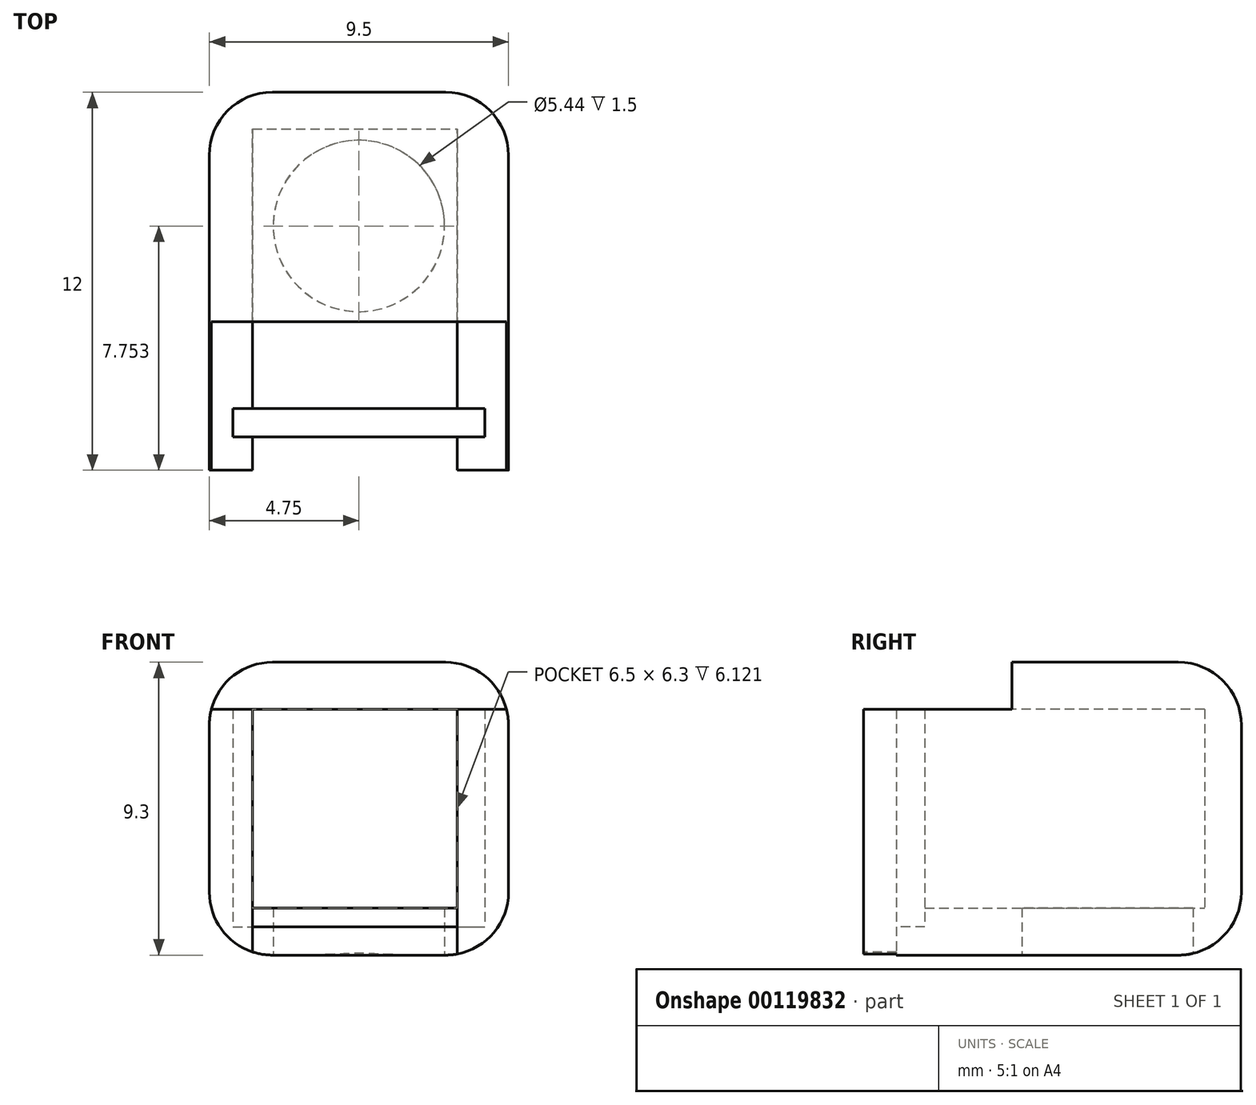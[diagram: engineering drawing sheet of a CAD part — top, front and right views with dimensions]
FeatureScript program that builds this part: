
annotation { "Feature Type Name" : "Feature", "Feature Type Description" : "" }
export const myFeature = defineFeature(function(context is Context, id is Id, definition is map)
    precondition{}
    {
        {
            var Q0;
            Q0=qCreatedBy(makeId("Top.planeOp"),FACE);
            var sketch = newSketch(context, id + "F0", { "sketchPlane" : qUnion([Q0])});
            skPoint(sketch, "E0.rect.middle", {"position": v(0, 0) * mm});
            skLineSegment(sketch, "E1.rect.bottom", {"start": v(-4.75, -1.5) * mm, "end": v(4.75, -1.5) * mm});
            skLineSegment(sketch, "E1.rect.top", {"start": v(-4.75, 1.5) * mm, "end": v(-3.38, 1.5) * mm});
            skLineSegment(sketch, "E1.rect.left", {"start": v(-4.75, -1.5) * mm, "end": v(-4.75, 1.5) * mm});
            skLineSegment(sketch, "E1.rect.right", {"start": v(4.75, -1.5) * mm, "end": v(4.75, 1.5) * mm});
            skLineSegment(sketch, "E2.rect.bottom", {"start": v(4, -0.45) * mm, "end": v(-4, -0.45) * mm});
            skLineSegment(sketch, "E2.rect.top", {"start": v(4, 0.45) * mm, "end": v(-4, 0.45) * mm});
            skLineSegment(sketch, "E2.rect.left", {"start": v(4, -0.45) * mm, "end": v(4, 0.45) * mm});
            skLineSegment(sketch, "E2.rect.right", {"start": v(-4, -0.45) * mm, "end": v(-4, 0.45) * mm});
            skLineSegment(sketch, "E3.rect.bottom", {"start": v(-3.12, -1.5) * mm, "end": v(3.38, -1.5) * mm});
            skLineSegment(sketch, "E4.trimOffspring", {"start": v(3.12, 1.5) * mm, "end": v(4.75, 1.5) * mm});
            skLineSegment(sketch, "E5", {"start": v(-3.38, 1.5) * mm, "end": v(3.12, 1.5) * mm, "construction": true});
            skLineSegment(sketch, "E6.bottom", {"start": v(4.75, 1.5) * mm, "end": v(-4.75, 1.5) * mm});
            skLineSegment(sketch, "E7.bottom", {"start": v(3.12, 1.5) * mm, "end": v(-4.75, 1.5) * mm});
            skLineSegment(sketch, "E8.bottom", {"start": v(-4.75, 1.5) * mm, "end": v(4.75, 1.5) * mm});
            skLineSegment(sketch, "E8.top", {"start": v(-4.75, 10.5) * mm, "end": v(4.75, 10.5) * mm});
            skLineSegment(sketch, "E8.left", {"start": v(-4.75, 1.5) * mm, "end": v(-4.75, 10.5) * mm});
            skLineSegment(sketch, "E8.right", {"start": v(4.75, 1.5) * mm, "end": v(4.75, 10.5) * mm});
            skLineSegment(sketch, "E9", {"start": v(-3.38, 1.5) * mm, "end": v(-3.38, 10.5) * mm});
            skLineSegment(sketch, "E10", {"start": v(3.12, 1.5) * mm, "end": v(3.12, 10.5) * mm});
            skLineSegment(sketch, "E11", {"start": v(4.75, 9.33) * mm, "end": v(-4.75, 9.33) * mm});
            skLineSegment(sketch, "E12", {"start": v(-3.38, 1.5) * mm, "end": v(-3.38, -1.5) * mm});
            skLineSegment(sketch, "E13", {"start": v(3.12, 1.5) * mm, "end": v(3.12, -1.5) * mm});
            skSolve(sketch);
        }
        {
            var Q0;
            {var subQ0=sQuery(id+"F0.wireOp",EDGE,"E6.right");Q0=makeQuery(id+"F0.imprint","IMPRINT",FACE,{"disambiguationData":[TD([[makeQuery(id+"F0.imprint","IMPRINT",EDGE,{"derivedFrom":subQ0}),-1.0]])]});}
            var Q1;
            Q1=makeQuery(id+"F0.imprint","IMPRINT",FACE,{"disambiguationData":[TD([[makeQuery(id+"F0.imprint","IMPRINT",EDGE,{"derivedFrom":sQuery(id+"F0.wireOp",EDGE,"E7.bottom")}),-1.0]])]});
            var Q2;
            {var subQ5=sQuery(id+"F0.wireOp",EDGE,"E7.bottom");Q2=makeQuery(id+"F0.imprint","IMPRINT",FACE,{"disambiguationData":[TD([[makeQuery(id+"F0.imprint","IMPRINT",EDGE,{"derivedFrom":subQ5}),1.0]])]});}
            var Q3;
            {var subQ8=sQuery(id+"F0.wireOp",EDGE,"E1.rect.right");Q3=makeQuery(id+"F0.imprint","IMPRINT",FACE,{"disambiguationData":[TD([[makeQuery(id+"F0.imprint","IMPRINT",EDGE,{"derivedFrom":subQ8}),1.0]])]});}
            var Q4;
            {var subQ5=sQuery(id+"F0.wireOp",EDGE,"E3.rect.bottom");Q4=makeQuery(id+"F0.imprint","IMPRINT",FACE,{"disambiguationData":[TD([[makeQuery(id+"F0.imprint","IMPRINT",EDGE,{"derivedFrom":subQ5}),1.0]])]});}
            var Q5;
            {var subQ4=sQuery(id+"F0.wireOp",EDGE,"E1.rect.left");Q5=makeQuery(id+"F0.imprint","IMPRINT",FACE,{"disambiguationData":[TD([[makeQuery(id+"F0.imprint","IMPRINT",EDGE,{"derivedFrom":subQ4}),-1.0]])]});}
            var Q6;
            {var subQ0=sQuery(id+"F0.wireOp",EDGE,"E6.left");Q6=makeQuery(id+"F0.imprint","IMPRINT",FACE,{"disambiguationData":[TD([[makeQuery(id+"F0.imprint","IMPRINT",EDGE,{"derivedFrom":subQ0}),1.0]])]});}
            var Q7;
            {var subQ0=sQuery(id+"F0.wireOp",EDGE,"E3.rect.right");var subQ1=sQuery(id+"F0.wireOp",EDGE,"E2.rect.bottom");var subQ2=makeQuery(id+"F0.imprint","INTERSECT",VERTEX,{"derivedFrom":[subQ1,subQ0]});Q7=makeQuery(id+"F0.imprint","IMPRINT",FACE,{"disambiguationData":[TD([[makeQuery(id+"F0.imprint","IMPRINT",EDGE,{"disambiguationData":[TD([[subQ2,-1.0]])],"derivedFrom":subQ1}),-1.0]])]});}
            var Q8;
            {var subQ0=sQuery(id+"F0.wireOp",EDGE,"E2.rect.right");Q8=makeQuery(id+"F0.imprint","IMPRINT",FACE,{"disambiguationData":[TD([[makeQuery(id+"F0.imprint","IMPRINT",EDGE,{"derivedFrom":subQ0}),-1.0]])]});}
            var Q9;
            {var subQ0=sQuery(id+"F0.wireOp",EDGE,"E2.rect.left");Q9=makeQuery(id+"F0.imprint","IMPRINT",FACE,{"disambiguationData":[TD([[makeQuery(id+"F0.imprint","IMPRINT",EDGE,{"derivedFrom":subQ0}),1.0]])]});}
            var Q10;
            {var subQ0=sQuery(id+"F0.wireOp",EDGE,"E8.left");var subQ5=sQuery(id+"F0.wireOp",EDGE,"E11");var subQ6=makeQuery(id+"F0.imprint","INTERSECT",VERTEX,{"derivedFrom":[subQ0,subQ5]});Q10=makeQuery(id+"F0.imprint","IMPRINT",FACE,{"disambiguationData":[TD([[makeQuery(id+"F0.imprint","IMPRINT",EDGE,{"disambiguationData":[TD([[subQ6,1.0]])],"derivedFrom":subQ5}),1.0]])]});}
            var Q11;
            {var subQ0=sQuery(id+"F0.wireOp",EDGE,"E8.left");var subQ1=sQuery(id+"F0.wireOp",EDGE,"E8.top");var subQ2=makeQuery(id+"F0.imprint","INTERSECT",VERTEX,{"derivedFrom":[subQ1,subQ0]});Q11=makeQuery(id+"F0.imprint","IMPRINT",FACE,{"disambiguationData":[TD([[makeQuery(id+"F0.imprint","IMPRINT",EDGE,{"disambiguationData":[TD([[subQ2,-1.0]])],"derivedFrom":subQ1}),-1.0]])]});}
            var Q12;
            {var subQ0=sQuery(id+"F0.wireOp",EDGE,"E9");var subQ1=sQuery(id+"F0.wireOp",EDGE,"E8.top");var subQ2=makeQuery(id+"F0.imprint","INTERSECT",VERTEX,{"derivedFrom":[subQ1,subQ0]});Q12=makeQuery(id+"F0.imprint","IMPRINT",FACE,{"disambiguationData":[TD([[makeQuery(id+"F0.imprint","IMPRINT",EDGE,{"disambiguationData":[TD([[subQ2,-1.0]])],"derivedFrom":subQ1}),-1.0]])]});}
            var Q13;
            {var subQ0=sQuery(id+"F0.wireOp",EDGE,"E8.right");var subQ1=sQuery(id+"F0.wireOp",EDGE,"E8.top");var subQ2=makeQuery(id+"F0.imprint","INTERSECT",VERTEX,{"derivedFrom":[subQ1,subQ0]});Q13=makeQuery(id+"F0.imprint","IMPRINT",FACE,{"disambiguationData":[TD([[makeQuery(id+"F0.imprint","IMPRINT",EDGE,{"disambiguationData":[TD([[subQ2,1.0]])],"derivedFrom":subQ1}),-1.0]])]});}
            var Q14;
            {var subQ0=sQuery(id+"F0.wireOp",EDGE,"E8.right");var subQ5=sQuery(id+"F0.wireOp",EDGE,"E11");var subQ6=makeQuery(id+"F0.imprint","INTERSECT",VERTEX,{"derivedFrom":[subQ0,subQ5]});Q14=makeQuery(id+"F0.imprint","IMPRINT",FACE,{"disambiguationData":[TD([[makeQuery(id+"F0.imprint","IMPRINT",EDGE,{"disambiguationData":[TD([[subQ6,-1.0]])],"derivedFrom":subQ5}),1.0]])]});}
            var Q15;
            {var subQ0=sQuery(id+"F0.wireOp",EDGE,"E3.rect.right");var subQ1=sQuery(id+"F0.wireOp",EDGE,"E2.rect.top");var subQ2=makeQuery(id+"F0.imprint","INTERSECT",VERTEX,{"derivedFrom":[subQ1,subQ0]});Q15=makeQuery(id+"F0.imprint","IMPRINT",FACE,{"disambiguationData":[TD([[makeQuery(id+"F0.imprint","IMPRINT",EDGE,{"disambiguationData":[TD([[subQ2,-1.0]])],"derivedFrom":subQ1}),-1.0]])]});}
            var Q16;
            {var subQ0=sQuery(id+"F0.wireOp",EDGE,"E9");var subQ5=sQuery(id+"F0.wireOp",EDGE,"E11");var subQ6=makeQuery(id+"F0.imprint","INTERSECT",VERTEX,{"derivedFrom":[subQ0,subQ5]});Q16=makeQuery(id+"F0.imprint","IMPRINT",FACE,{"disambiguationData":[TD([[makeQuery(id+"F0.imprint","IMPRINT",EDGE,{"disambiguationData":[TD([[subQ6,1.0]])],"derivedFrom":subQ5}),1.0]])]});}
            extrude(context, id + "F1", {"entities" : qUnion([Q0, Q1, Q2, Q3, Q4, Q5, Q6, Q7, Q8, Q9, Q10, Q11, Q12, Q13, Q14, Q15, Q16]), "depth" : 0.9 * mm});
        }
        {
            var Q0;
            {var subQ0=sQuery(id+"F0.wireOp",EDGE,"E6.left");Q0=makeQuery(id+"F0.imprint","IMPRINT",FACE,{"disambiguationData":[TD([[makeQuery(id+"F0.imprint","IMPRINT",EDGE,{"derivedFrom":subQ0}),1.0]])]});}
            var Q1;
            {var subQ0=sQuery(id+"F0.wireOp",EDGE,"E6.right");Q1=makeQuery(id+"F0.imprint","IMPRINT",FACE,{"disambiguationData":[TD([[makeQuery(id+"F0.imprint","IMPRINT",EDGE,{"derivedFrom":subQ0}),-1.0]])]});}
            var Q2;
            {var subQ5=sQuery(id+"F0.wireOp",EDGE,"E3.rect.bottom");Q2=makeQuery(id+"F0.imprint","IMPRINT",FACE,{"disambiguationData":[TD([[makeQuery(id+"F0.imprint","IMPRINT",EDGE,{"derivedFrom":subQ5}),1.0]])]});}
            var Q3;
            {var subQ4=sQuery(id+"F0.wireOp",EDGE,"E1.rect.left");Q3=makeQuery(id+"F0.imprint","IMPRINT",FACE,{"disambiguationData":[TD([[makeQuery(id+"F0.imprint","IMPRINT",EDGE,{"derivedFrom":subQ4}),-1.0]])]});}
            var Q4;
            {var subQ8=sQuery(id+"F0.wireOp",EDGE,"E1.rect.right");Q4=makeQuery(id+"F0.imprint","IMPRINT",FACE,{"disambiguationData":[TD([[makeQuery(id+"F0.imprint","IMPRINT",EDGE,{"derivedFrom":subQ8}),1.0]])]});}
            var Q5;
            {var subQ5=sQuery(id+"F0.wireOp",EDGE,"E7.bottom");Q5=makeQuery(id+"F0.imprint","IMPRINT",FACE,{"disambiguationData":[TD([[makeQuery(id+"F0.imprint","IMPRINT",EDGE,{"derivedFrom":subQ5}),1.0]])]});}
            var Q6;
            {var subQ0=sQuery(id+"F0.wireOp",EDGE,"E8.right");var subQ5=sQuery(id+"F0.wireOp",EDGE,"E11");var subQ6=makeQuery(id+"F0.imprint","INTERSECT",VERTEX,{"derivedFrom":[subQ0,subQ5]});Q6=makeQuery(id+"F0.imprint","IMPRINT",FACE,{"disambiguationData":[TD([[makeQuery(id+"F0.imprint","IMPRINT",EDGE,{"disambiguationData":[TD([[subQ6,-1.0]])],"derivedFrom":subQ5}),1.0]])]});}
            var Q7;
            {var subQ0=sQuery(id+"F0.wireOp",EDGE,"E3.rect.right");var subQ1=sQuery(id+"F0.wireOp",EDGE,"E2.rect.top");var subQ2=makeQuery(id+"F0.imprint","INTERSECT",VERTEX,{"derivedFrom":[subQ1,subQ0]});Q7=makeQuery(id+"F0.imprint","IMPRINT",FACE,{"disambiguationData":[TD([[makeQuery(id+"F0.imprint","IMPRINT",EDGE,{"disambiguationData":[TD([[subQ2,-1.0]])],"derivedFrom":subQ1}),-1.0]])]});}
            var Q8;
            {var subQ0=sQuery(id+"F0.wireOp",EDGE,"E9");var subQ5=sQuery(id+"F0.wireOp",EDGE,"E11");var subQ6=makeQuery(id+"F0.imprint","INTERSECT",VERTEX,{"derivedFrom":[subQ0,subQ5]});Q8=makeQuery(id+"F0.imprint","IMPRINT",FACE,{"disambiguationData":[TD([[makeQuery(id+"F0.imprint","IMPRINT",EDGE,{"disambiguationData":[TD([[subQ6,1.0]])],"derivedFrom":subQ5}),1.0]])]});}
            var Q9;
            {var subQ0=sQuery(id+"F0.wireOp",EDGE,"E8.left");var subQ5=sQuery(id+"F0.wireOp",EDGE,"E11");var subQ6=makeQuery(id+"F0.imprint","INTERSECT",VERTEX,{"derivedFrom":[subQ0,subQ5]});Q9=makeQuery(id+"F0.imprint","IMPRINT",FACE,{"disambiguationData":[TD([[makeQuery(id+"F0.imprint","IMPRINT",EDGE,{"disambiguationData":[TD([[subQ6,1.0]])],"derivedFrom":subQ5}),1.0]])]});}
            var Q10;
            {var subQ0=sQuery(id+"F0.wireOp",EDGE,"E8.left");var subQ1=sQuery(id+"F0.wireOp",EDGE,"E8.top");var subQ2=makeQuery(id+"F0.imprint","INTERSECT",VERTEX,{"derivedFrom":[subQ1,subQ0]});Q10=makeQuery(id+"F0.imprint","IMPRINT",FACE,{"disambiguationData":[TD([[makeQuery(id+"F0.imprint","IMPRINT",EDGE,{"disambiguationData":[TD([[subQ2,-1.0]])],"derivedFrom":subQ1}),-1.0]])]});}
            var Q11;
            {var subQ0=sQuery(id+"F0.wireOp",EDGE,"E9");var subQ1=sQuery(id+"F0.wireOp",EDGE,"E8.top");var subQ2=makeQuery(id+"F0.imprint","INTERSECT",VERTEX,{"derivedFrom":[subQ1,subQ0]});Q11=makeQuery(id+"F0.imprint","IMPRINT",FACE,{"disambiguationData":[TD([[makeQuery(id+"F0.imprint","IMPRINT",EDGE,{"disambiguationData":[TD([[subQ2,-1.0]])],"derivedFrom":subQ1}),-1.0]])]});}
            var Q12;
            {var subQ0=sQuery(id+"F0.wireOp",EDGE,"E8.right");var subQ1=sQuery(id+"F0.wireOp",EDGE,"E8.top");var subQ2=makeQuery(id+"F0.imprint","INTERSECT",VERTEX,{"derivedFrom":[subQ1,subQ0]});Q12=makeQuery(id+"F0.imprint","IMPRINT",FACE,{"disambiguationData":[TD([[makeQuery(id+"F0.imprint","IMPRINT",EDGE,{"disambiguationData":[TD([[subQ2,1.0]])],"derivedFrom":subQ1}),-1.0]])]});}
            extrude(context, id + "F2", {"entities" : qUnion([Q0, Q1, Q2, Q3, Q4, Q5, Q6, Q7, Q8, Q9, Q10, Q11, Q12]), "operationType" : NewBodyOperationType.ADD, "depth" : 1.5 * mm});
        }
        {
            var Q0;
            {var subQ9=sQuery(id+"F0.wireOp",EDGE,"E1.rect.top");Q0=makeQuery(id+"F0.imprint","IMPRINT",FACE,{"disambiguationData":[TD([[makeQuery(id+"F0.imprint","IMPRINT",EDGE,{"derivedFrom":subQ9}),-1.0]])]});}
            var Q1;
            {var subQ4=sQuery(id+"F0.wireOp",EDGE,"E1.rect.right");Q1=makeQuery(id+"F0.imprint","IMPRINT",FACE,{"disambiguationData":[TD([[makeQuery(id+"F0.imprint","IMPRINT",EDGE,{"derivedFrom":subQ4}),1.0]])]});}
            var Q2;
            {var subQ4=sQuery(id+"F0.wireOp",EDGE,"E1.rect.left");Q2=makeQuery(id+"F0.imprint","IMPRINT",FACE,{"disambiguationData":[TD([[makeQuery(id+"F0.imprint","IMPRINT",EDGE,{"derivedFrom":subQ4}),-1.0]])]});}
            var Q3;
            {var subQ0=sQuery(id+"F0.wireOp",EDGE,"E6.right");Q3=makeQuery(id+"F0.imprint","IMPRINT",FACE,{"disambiguationData":[TD([[makeQuery(id+"F0.imprint","IMPRINT",EDGE,{"derivedFrom":subQ0}),-1.0]])]});}
            var Q4;
            {var subQ0=sQuery(id+"F0.wireOp",EDGE,"E6.left");Q4=makeQuery(id+"F0.imprint","IMPRINT",FACE,{"disambiguationData":[TD([[makeQuery(id+"F0.imprint","IMPRINT",EDGE,{"derivedFrom":subQ0}),1.0]])]});}
            var Q5;
            {var subQ0=sQuery(id+"F0.wireOp",EDGE,"E8.left");var subQ5=sQuery(id+"F0.wireOp",EDGE,"E11");var subQ6=makeQuery(id+"F0.imprint","INTERSECT",VERTEX,{"derivedFrom":[subQ0,subQ5]});Q5=makeQuery(id+"F0.imprint","IMPRINT",FACE,{"disambiguationData":[TD([[makeQuery(id+"F0.imprint","IMPRINT",EDGE,{"disambiguationData":[TD([[subQ6,1.0]])],"derivedFrom":subQ5}),1.0]])]});}
            var Q6;
            {var subQ0=sQuery(id+"F0.wireOp",EDGE,"E8.right");var subQ5=sQuery(id+"F0.wireOp",EDGE,"E11");var subQ6=makeQuery(id+"F0.imprint","INTERSECT",VERTEX,{"derivedFrom":[subQ0,subQ5]});Q6=makeQuery(id+"F0.imprint","IMPRINT",FACE,{"disambiguationData":[TD([[makeQuery(id+"F0.imprint","IMPRINT",EDGE,{"disambiguationData":[TD([[subQ6,-1.0]])],"derivedFrom":subQ5}),1.0]])]});}
            var Q7;
            {var subQ0=sQuery(id+"F0.wireOp",EDGE,"E8.left");var subQ1=sQuery(id+"F0.wireOp",EDGE,"E8.top");var subQ2=makeQuery(id+"F0.imprint","INTERSECT",VERTEX,{"derivedFrom":[subQ1,subQ0]});Q7=makeQuery(id+"F0.imprint","IMPRINT",FACE,{"disambiguationData":[TD([[makeQuery(id+"F0.imprint","IMPRINT",EDGE,{"disambiguationData":[TD([[subQ2,-1.0]])],"derivedFrom":subQ1}),-1.0]])]});}
            var Q8;
            {var subQ0=sQuery(id+"F0.wireOp",EDGE,"E9");var subQ1=sQuery(id+"F0.wireOp",EDGE,"E8.top");var subQ2=makeQuery(id+"F0.imprint","INTERSECT",VERTEX,{"derivedFrom":[subQ1,subQ0]});Q8=makeQuery(id+"F0.imprint","IMPRINT",FACE,{"disambiguationData":[TD([[makeQuery(id+"F0.imprint","IMPRINT",EDGE,{"disambiguationData":[TD([[subQ2,-1.0]])],"derivedFrom":subQ1}),-1.0]])]});}
            var Q9;
            {var subQ0=sQuery(id+"F0.wireOp",EDGE,"E8.right");var subQ1=sQuery(id+"F0.wireOp",EDGE,"E8.top");var subQ2=makeQuery(id+"F0.imprint","INTERSECT",VERTEX,{"derivedFrom":[subQ1,subQ0]});Q9=makeQuery(id+"F0.imprint","IMPRINT",FACE,{"disambiguationData":[TD([[makeQuery(id+"F0.imprint","IMPRINT",EDGE,{"disambiguationData":[TD([[subQ2,1.0]])],"derivedFrom":subQ1}),-1.0]])]});}
            extrude(context, id + "F3", {"entities" : qUnion([Q0, Q1, Q2, Q3, Q4, Q5, Q6, Q7, Q8, Q9]), "operationType" : NewBodyOperationType.ADD, "depth" : 7.8 * mm});
        }
        {
            var Q0;
            Q0=makeQuery(id+"F3.opExtrude","CAP_FACE",FACE,{"disambiguationData":[OSD([sQuery(id+"F0.wireOp",EDGE,"E1.rect.bottom"),sQuery(id+"F0.wireOp",EDGE,"E1.rect.left"),sQuery(id+"F0.wireOp",EDGE,"E1.rect.right"),sQuery(id+"F0.wireOp",EDGE,"E2.rect.bottom"),sQuery(id+"F0.wireOp",EDGE,"E2.rect.top"),sQuery(id+"F0.wireOp",EDGE,"E2.rect.left"),sQuery(id+"F0.wireOp",EDGE,"E2.rect.right"),sQuery(id+"F0.wireOp",EDGE,"E3.rect.left"),sQuery(id+"F0.wireOp",EDGE,"E3.rect.right"),sQuery(id+"F0.wireOp",EDGE,"E8.top"),sQuery(id+"F0.wireOp",EDGE,"E8.left"),sQuery(id+"F0.wireOp",EDGE,"E8.right"),sQuery(id+"F0.wireOp",EDGE,"E9"),sQuery(id+"F0.wireOp",EDGE,"E10"),sQuery(id+"F0.wireOp",EDGE,"E11")])],"isStart":false});
            cPlane(context, id + "F4", {"entities" : qUnion([Q0]), "cplaneType" : CPlaneType.OFFSET, "offset" : 0 * mm, "width" : 150 * mm, "height" : 150 * mm});
        }
        {
            var Q0;
            Q0=qCreatedBy(id+"F4.planeOp",FACE);
            var sketch = newSketch(context, id + "F5", { "sketchPlane" : qUnion([Q0])});
            skLineSegment(sketch, "E14.top", {"start": v(4.75, -1.5) * mm, "end": v(-4.75, -1.5) * mm});
            skLineSegment(sketch, "E14.left", {"start": v(4.75, 1.5) * mm, "end": v(4.75, -1.5) * mm});
            skLineSegment(sketch, "E14.right", {"start": v(-4.75, 1.5) * mm, "end": v(-4.75, -1.5) * mm});
            skPoint(sketch, "E14.middle", {"position": v(0, 0) * mm});
            skLineSegment(sketch, "E15.bottom", {"start": v(4.75, 1.5) * mm, "end": v(-4.75, 1.5) * mm});
            skLineSegment(sketch, "E15.top", {"start": v(4.75, 10.5) * mm, "end": v(-4.75, 10.5) * mm});
            skLineSegment(sketch, "E15.left", {"start": v(4.75, 1.5) * mm, "end": v(4.75, 10.5) * mm});
            skLineSegment(sketch, "E15.right", {"start": v(-4.75, 1.5) * mm, "end": v(-4.75, 10.5) * mm});
            skLineSegment(sketch, "E16", {"start": v(4.75, 3.21) * mm, "end": v(-4.75, 3.21) * mm});
            skSolve(sketch);
        }
        {
            var Q0;
            {var subQ0=sQuery(id+"F5.wireOp",EDGE,"E15.top");Q0=makeQuery(id+"F5.imprint","IMPRINT",FACE,{"disambiguationData":[TD([[makeQuery(id+"F5.imprint","IMPRINT",EDGE,{"derivedFrom":subQ0}),1.0]])]});}
            extrude(context, id + "F6", {"entities" : qUnion([Q0]), "operationType" : NewBodyOperationType.ADD, "depth" : 1.5 * mm});
        }
        {
            var Q0;
            Q0=qCreatedBy(makeId("Front.planeOp"),FACE);
            var sketch = newSketch(context, id + "F7", { "sketchPlane" : qUnion([Q0])});
            skLineSegment(sketch, "E17", {"start": v(0, 0) * mm, "end": v(0, 9) * mm, "construction": true});
            skCircle(sketch, "E18", {"center": v(0, 4.5) * mm, "radius": 3 * mm});
            skSolve(sketch);
        }
        {
            var Q0;
            Q0=qSketchRegion(id+"F7",true);
            extrude(context, id + "F8", {"entities" : qUnion([Q0]), "operationType" : NewBodyOperationType.REMOVE, "oppositeDirection" : true, "depth" : 9 * mm});
        }
        {
            var Q0;
            {var subQ0=sQuery(id+"F0.wireOp",EDGE,"E8.right");var subQ1=sQuery(id+"F0.wireOp",EDGE,"E8.top");Q0=makeQuery(id+"F6.boolean.opBoolean","MERGE",EDGE,{"derivedFrom":[makeQuery(id+"F3.boolean.opBoolean","MERGE",EDGE,{"derivedFrom":[makeQuery(id+"F2.boolean.opBoolean","MERGE",EDGE,{"derivedFrom":[makeQuery(id+"F1.opExtrude","SWEPT_EDGE",EDGE,{"disambiguationData":[OSD([subQ1,subQ0])]}),makeQuery(id+"F2.opExtrude","SWEPT_EDGE",EDGE,{"disambiguationData":[OSD([subQ1,subQ0])]})]}),makeQuery(id+"F3.opExtrude","SWEPT_EDGE",EDGE,{"disambiguationData":[OSD([subQ1,subQ0])]})]}),makeQuery(id+"F6.opExtrude","SWEPT_EDGE",EDGE,{"disambiguationData":[OSD([sQuery(id+"F5.wireOp",EDGE,"E15.top"),sQuery(id+"F5.wireOp",EDGE,"E15.left")])]})]});}
            var Q1;
            Q1=makeQuery(id+"F6.opExtrude","CAP_EDGE",EDGE,{"disambiguationData":[OSD([sQuery(id+"F5.wireOp",EDGE,"E15.top")])],"isStart":false});
            var Q2;
            Q2=makeQuery(id+"F6.opExtrude","CAP_EDGE",EDGE,{"disambiguationData":[OSD([sQuery(id+"F5.wireOp",EDGE,"E15.left")])],"isStart":false});
            var Q3;
            Q3=makeQuery(id+"F1.opExtrude","CAP_EDGE",EDGE,{"disambiguationData":[OSD([sQuery(id+"F0.wireOp",EDGE,"E1.rect.right"),sQuery(id+"F0.wireOp",EDGE,"E8.right")])],"isStart":true});
            var Q4;
            Q4=makeQuery(id+"F1.opExtrude","CAP_EDGE",EDGE,{"disambiguationData":[OSD([sQuery(id+"F0.wireOp",EDGE,"E8.top")])],"isStart":true});
            var Q5;
            Q5=makeQuery(id+"F1.opExtrude","CAP_EDGE",EDGE,{"disambiguationData":[OSD([sQuery(id+"F0.wireOp",EDGE,"E1.rect.left"),sQuery(id+"F0.wireOp",EDGE,"E8.left")])],"isStart":true});
            var Q6;
            {var subQ0=sQuery(id+"F0.wireOp",EDGE,"E8.left");var subQ1=sQuery(id+"F0.wireOp",EDGE,"E8.top");Q6=makeQuery(id+"F6.boolean.opBoolean","MERGE",EDGE,{"derivedFrom":[makeQuery(id+"F3.boolean.opBoolean","MERGE",EDGE,{"derivedFrom":[makeQuery(id+"F2.boolean.opBoolean","MERGE",EDGE,{"derivedFrom":[makeQuery(id+"F1.opExtrude","SWEPT_EDGE",EDGE,{"disambiguationData":[OSD([subQ1,subQ0])]}),makeQuery(id+"F2.opExtrude","SWEPT_EDGE",EDGE,{"disambiguationData":[OSD([subQ1,subQ0])]})]}),makeQuery(id+"F3.opExtrude","SWEPT_EDGE",EDGE,{"disambiguationData":[OSD([subQ1,subQ0])]})]}),makeQuery(id+"F6.opExtrude","SWEPT_EDGE",EDGE,{"disambiguationData":[OSD([sQuery(id+"F5.wireOp",EDGE,"E15.top"),sQuery(id+"F5.wireOp",EDGE,"E15.right")])]})]});}
            var Q7;
            Q7=makeQuery(id+"F6.opExtrude","CAP_EDGE",EDGE,{"disambiguationData":[OSD([sQuery(id+"F5.wireOp",EDGE,"E15.right")])],"isStart":false});
            fillet(context, id + "F9", {"entities" : qUnion([Q0, Q1, Q2, Q3, Q4, Q5, Q6, Q7]), "radius" : 2 * mm, "tangentPropagation" : true, "allowEdgeOverflow" : false});
        }
        {
            var Q0;
            Q0=qCreatedBy(makeId("Top.planeOp"),FACE);
            var sketch = newSketch(context, id + "F10", { "sketchPlane" : qUnion([Q0])});
            skCircle(sketch, "E19", {"center": v(0, 6.25) * mm, "radius": 2.72 * mm});
            skSolve(sketch);
        }
        {
            var Q0;
            Q0=qSketchRegion(id+"F10",true);
            extrude(context, id + "F11", {"entities" : qUnion([Q0]), "operationType" : NewBodyOperationType.REMOVE, "depth" : 6 * mm});
        }
    });
